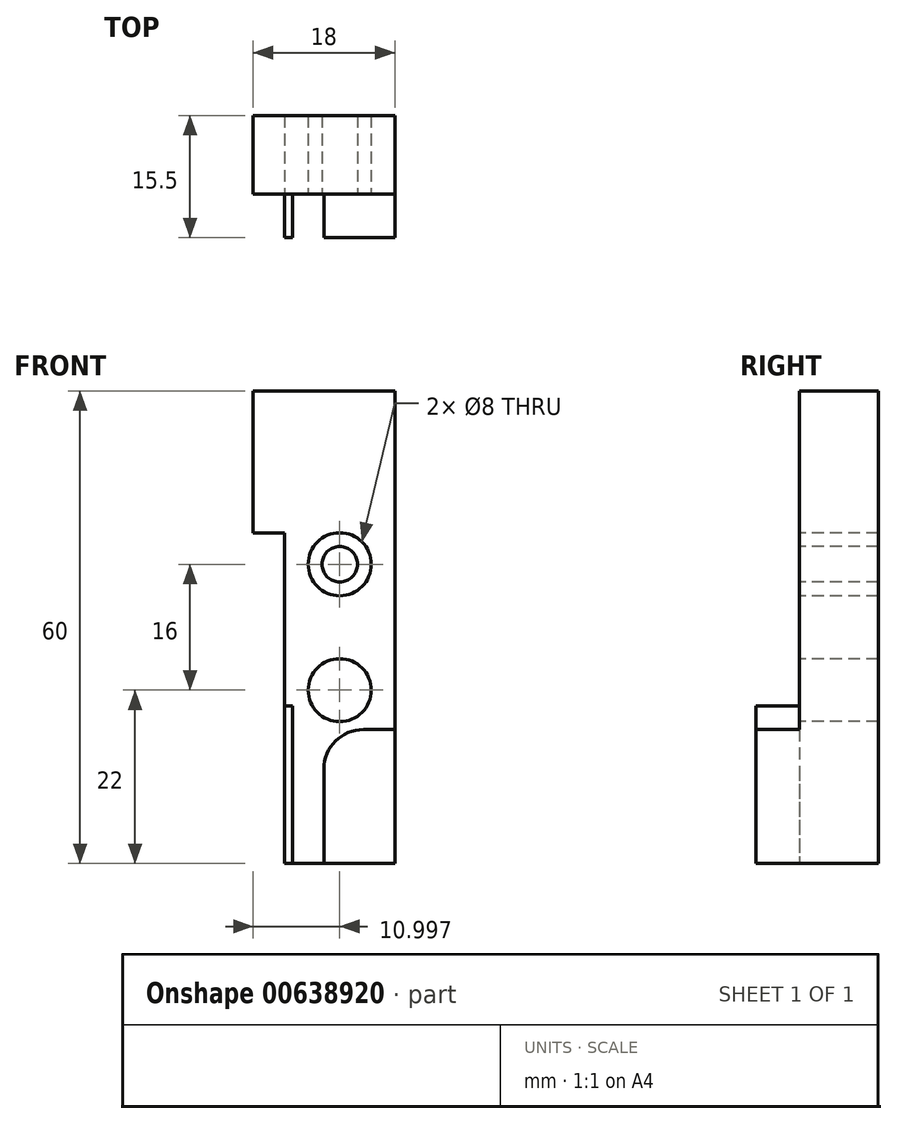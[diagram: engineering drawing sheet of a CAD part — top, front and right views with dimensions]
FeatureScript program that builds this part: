
annotation { "Feature Type Name" : "Feature", "Feature Type Description" : "" }
export const myFeature = defineFeature(function(context is Context, id is Id, definition is map)
    precondition{}
    {
        {
            var Q0;
            Q0=qCreatedBy(makeId("Front.planeOp"),FACE);
            var sketch = newSketch(context, id + "F0", { "sketchPlane" : qUnion([Q0])});
            skLineSegment(sketch, "E0", {"start": v(16.2, 30) * mm, "end": v(16.2, -30) * mm});
            skLineSegment(sketch, "E1", {"start": v(31.7, 30) * mm, "end": v(31.7, -30) * mm});
            skLineSegment(sketch, "E2", {"start": v(16.2, 30) * mm, "end": v(31.7, 30) * mm});
            skLineSegment(sketch, "E3", {"start": v(16.2, -30) * mm, "end": v(31.7, -30) * mm});
            skLineSegment(sketch, "E4", {"start": v(-27.7, 12) * mm, "end": v(-27.7, -30) * mm});
            skLineSegment(sketch, "E5", {"start": v(-31.7, 12) * mm, "end": v(-27.7, 12) * mm});
            skLineSegment(sketch, "E6", {"start": v(-31.7, 30) * mm, "end": v(-31.7, 12) * mm});
            skLineSegment(sketch, "E7", {"start": v(-13.7, 30) * mm, "end": v(-31.7, 30) * mm});
            skCircle(sketch, "E8", {"center": v(-20.7, -8) * mm, "radius": 4 * mm});
            skCircle(sketch, "E9", {"center": v(-20.7, -8) * mm, "radius": 2.25 * mm});
            skCircle(sketch, "E10", {"center": v(-20.7, 8) * mm, "radius": 2.25 * mm});
            skCircle(sketch, "E11", {"center": v(-20.7, 8) * mm, "radius": 4 * mm});
            skLineSegment(sketch, "E12", {"start": v(-13.7, -30) * mm, "end": v(-27.7, -30) * mm});
            skLineSegment(sketch, "E13", {"start": v(-13.7, 30) * mm, "end": v(-13.7, -30) * mm});
            skLineSegment(sketch, "E14", {"start": v(-17.7, -13) * mm, "end": v(-13.7, -13) * mm});
            skArc(sketch, "E15", {"start": v(-17.7, -13) * mm, "mid": v(-21.23, -14.46) * mm, "end": v(-22.7, -18) * mm});
            skLineSegment(sketch, "E16", {"start": v(-22.7, -18) * mm, "end": v(-22.7, -30) * mm});
            skLineSegment(sketch, "E17", {"start": v(-26.7, -10) * mm, "end": v(-27.7, -10) * mm});
            skLineSegment(sketch, "E18", {"start": v(-26.7, -10) * mm, "end": v(-26.7, -30) * mm});
            skSolve(sketch);
        }
        {
            var Q0;
            {var subQ6=sQuery(id+"F0.wireOp",EDGE,"E5");Q0=makeQuery(id+"F0.imprint","IMPRINT",FACE,{"disambiguationData":[TD([[makeQuery(id+"F0.imprint","IMPRINT",EDGE,{"derivedFrom":subQ6}),1.0]])]});}
            var Q1;
            Q1=makeQuery(id+"F0.imprint","IMPRINT",FACE,{"disambiguationData":[TD([[makeQuery(id+"F0.imprint","IMPRINT",EDGE,{"derivedFrom":sQuery(id+"F0.wireOp",EDGE,"E10")}),1.0]])]});
            var Q2;
            Q2=makeQuery(id+"F0.imprint","IMPRINT",FACE,{"disambiguationData":[TD([[makeQuery(id+"F0.imprint","IMPRINT",EDGE,{"derivedFrom":sQuery(id+"F0.wireOp",EDGE,"E8")}),-1.0]])]});
            var Q3;
            {var subQ3=sQuery(id+"F0.wireOp",EDGE,"E14");Q3=makeQuery(id+"F0.imprint","IMPRINT",FACE,{"disambiguationData":[TD([[makeQuery(id+"F0.imprint","IMPRINT",EDGE,{"derivedFrom":subQ3}),-1.0]])]});}
            var Q4;
            Q4=makeQuery(id+"F0.imprint","IMPRINT",FACE,{"disambiguationData":[TD([[makeQuery(id+"F0.imprint","IMPRINT",EDGE,{"derivedFrom":sQuery(id+"F0.wireOp",EDGE,"E10")}),-1.0]])]});
            var Q5;
            {var subQ3=sQuery(id+"F0.wireOp",EDGE,"E17");Q5=makeQuery(id+"F0.imprint","IMPRINT",FACE,{"disambiguationData":[TD([[makeQuery(id+"F0.imprint","IMPRINT",EDGE,{"derivedFrom":subQ3}),1.0]])]});}
            var Q6;
            Q6=makeQuery(id+"F0.imprint","IMPRINT",FACE,{"disambiguationData":[TD([[makeQuery(id+"F0.imprint","IMPRINT",EDGE,{"derivedFrom":sQuery(id+"F0.wireOp",EDGE,"E9")}),-1.0]])]});
            extrude(context, id + "F1", {"entities" : qUnion([Q0, Q1, Q2, Q3, Q4, Q5, Q6]), "oppositeDirection" : true, "depth" : 15.5 * mm, "offsetDistance" : 25 * mm});
        }
        {
            var Q0;
            Q0=makeQuery(id+"F0.imprint","IMPRINT",FACE,{"disambiguationData":[TD([[makeQuery(id+"F0.imprint","IMPRINT",EDGE,{"derivedFrom":sQuery(id+"F0.wireOp",EDGE,"E10")}),-1.0]])]});
            var Q1;
            Q1=makeQuery(id+"F0.imprint","IMPRINT",FACE,{"disambiguationData":[TD([[makeQuery(id+"F0.imprint","IMPRINT",EDGE,{"derivedFrom":sQuery(id+"F0.wireOp",EDGE,"E9")}),-1.0]])]});
            extrude(context, id + "F2", {"entities" : qUnion([Q0, Q1]), "operationType" : NewBodyOperationType.REMOVE, "endBound" : BoundingType.THROUGH_ALL, "oppositeDirection" : true, "depth" : 25 * mm, "offsetDistance" : 25 * mm});
        }
        {
            var Q0;
            Q0=makeQuery(id+"F0.imprint","IMPRINT",FACE,{"disambiguationData":[TD([[makeQuery(id+"F0.imprint","IMPRINT",EDGE,{"derivedFrom":sQuery(id+"F0.wireOp",EDGE,"E10")}),1.0]])]});
            var Q1;
            Q1=makeQuery(id+"F0.imprint","IMPRINT",FACE,{"disambiguationData":[TD([[makeQuery(id+"F0.imprint","IMPRINT",EDGE,{"derivedFrom":sQuery(id+"F0.wireOp",EDGE,"E8")}),-1.0]])]});
            var Q2;
            Q2=makeQuery(id+"F0.imprint","IMPRINT",FACE,{"disambiguationData":[TD([[makeQuery(id+"F0.imprint","IMPRINT",EDGE,{"derivedFrom":sQuery(id+"F0.wireOp",EDGE,"E10")}),-1.0]])]});
            var Q3;
            Q3=makeQuery(id+"F0.imprint","IMPRINT",FACE,{"disambiguationData":[TD([[makeQuery(id+"F0.imprint","IMPRINT",EDGE,{"derivedFrom":sQuery(id+"F0.wireOp",EDGE,"E9")}),-1.0]])]});
            extrude(context, id + "F3", {"entities" : qUnion([Q0, Q1, Q2, Q3]), "operationType" : NewBodyOperationType.REMOVE, "oppositeDirection" : true, "depth" : 5.5 * mm, "offsetDistance" : 25 * mm});
        }
    });
